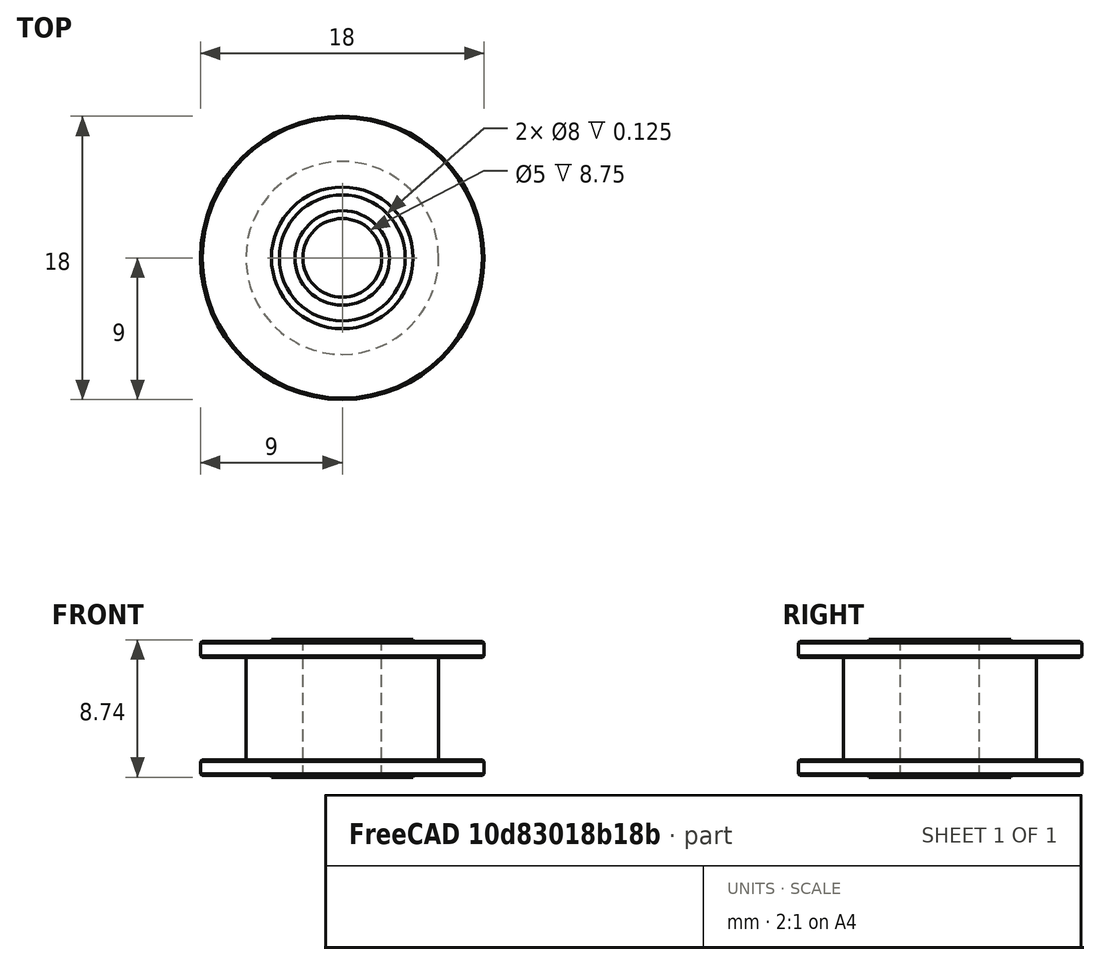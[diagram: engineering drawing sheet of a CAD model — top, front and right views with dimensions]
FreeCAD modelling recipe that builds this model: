
FCSTD DOCUMENT  (FreeCAD 0.17R12802 (Git))
Label: GT2_20T_Smooth_5mm_Bore
License: All rights reserved
LicenseURL: http://en.wikipedia.org/wiki/All_rights_reserved
objects: Part::Cylinder×10, Part::Cut×4, Part::Chamfer×2, Part::MultiFuse×1, Part::FeaturePython×1, App::DocumentObjectGroup×1, Part::Feature×1, App::Part×1
note: 19 computed .brp shape members not serialized (recipe doc carries the construction recipe); baked Part::Feature solids carry a one-line shape summary decoded from their .brp

FEATURE [Part::Cylinder] Cylinder003
  Angle = 360
  AttacherType = Attacher::AttachEngine3D
  Height = 8.75
  Placement = pos=(0,0,-0.125) rot=(0,0,1;0rad)
  Radius = 3
FEATURE [Part::Cylinder] Cylinder006
  Angle = 360
  AttacherType = Attacher::AttachEngine3D
  Height = 8.75
  Placement = pos=(0,0,-0.125) rot=(0,0,1;0rad)
  Radius = 4.5
FEATURE [Part::Cylinder] Cylinder002
  Angle = 360
  AttacherType = Attacher::AttachEngine3D
  Height = 6.5
  Placement = pos=(0,0,1) rot=(0,0,1;0rad)
  Radius = 6.125
FEATURE [Part::Cylinder] Cylinder008
  Angle = 360
  AttacherType = Attacher::AttachEngine3D
  Height = 8.75
  Placement = pos=(0,0,-0.125) rot=(0,0,1;0rad)
  Radius = 4.5
FEATURE [Part::Cylinder] Cylinder004
  Angle = 360
  AttacherType = Attacher::AttachEngine3D
  Height = 8.75
  Placement = pos=(0,0,-0.125) rot=(0,0,1;0rad)
  Radius = 2.5
FEATURE [Part::Cylinder] Cylinder007
  Angle = 360
  AttacherType = Attacher::AttachEngine3D
  Height = 8.75
  Placement = pos=(0,0,-0.125) rot=(0,0,1;0rad)
  Radius = 4
FEATURE [Part::Cut] Cut002
  Base = -> Cylinder008
  Tool = -> Cylinder007
FEATURE [Part::Cut] Cut003
  Base = -> Cylinder003
  Tool = -> Cylinder004
FEATURE [Part::Cylinder] Cylinder
  Angle = 360
  AttacherType = Attacher::AttachEngine3D
  Height = 1
  Radius = 9
FEATURE [Part::Chamfer] Chamfer
  Base = -> Cylinder
  Edges = 2 edges r=0.1: [Edge1,Edge3]
FEATURE [Part::Cylinder] Cylinder005
  Angle = 360
  AttacherType = Attacher::AttachEngine3D
  Height = 8.5
  Radius = 4
FEATURE [Part::Cylinder] Cylinder001
  Angle = 360
  AttacherType = Attacher::AttachEngine3D
  Height = 1
  Placement = pos=(0,0,7.5) rot=(0,0,1;0rad)
  Radius = 9
FEATURE [Part::Chamfer] Chamfer001
  Base = -> Cylinder001
  Edges = 2 edges r=0.1: [Edge1,Edge3]
FEATURE [Part::MultiFuse] Fusion
  Shapes = -> [Cylinder002,Chamfer001,Chamfer]
FEATURE [Part::Cut] Cut
  Base = -> Fusion
  Tool = -> Cylinder006
FEATURE [Part::Cylinder] Cylinder009
  Angle = 360
  AttacherType = Attacher::AttachEngine3D
  Height = 8.5
  Radius = 3
FEATURE [Part::Cut] Cut004
  Base = -> Cylinder005
  Tool = -> Cylinder009
FEATURE [Part::FeaturePython] Connect  # WARN: FeaturePython — macro-defined, semantics opaque (R4)
  Objects = -> [Cut,Cut003,Cut002,Cut004]
  Tolerance = 0
FEATURE [App::DocumentObjectGroup] Group  label="src"
  Group = -> [Cut004,Cut002,Cut003,Cut,Connect]
FEATURE [Part::Feature] Connect001  label="GT2 20T Smooth 5mm Bore final"
  shape: bbox 18 x 18 x 8.75 mm, 24 faces (baked)
FEATURE [App::Part] Part  label="GT2 20T Smooth 5mm Bore"
  Group = -> [Group,Cylinder005,Cylinder009,Cut004,Cylinder007,Cylinder008,Cut002,Cylinder003,Cylinder004,Cut003,Cylinder,Cylinder001,Cylinder002,Chamfer001,Chamfer,Cylinder006,Fusion,Cut,Connect,Connect001]
  License = CC BY 3.0
  LicenseURL = http://creativecommons.org/licenses/by/3.0/
  Origin = -> Origin
